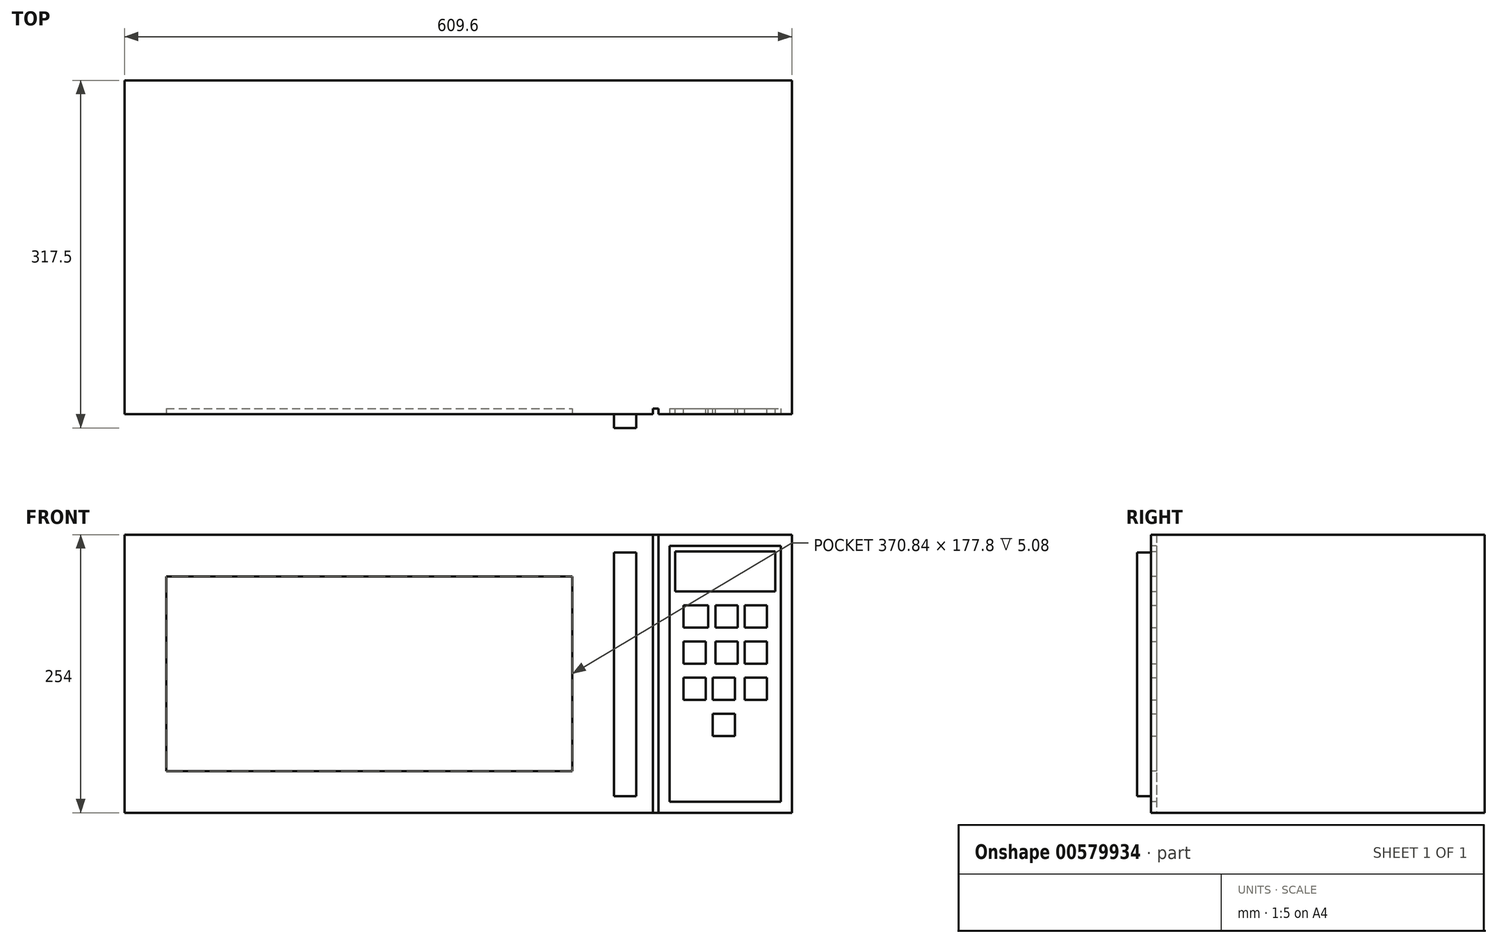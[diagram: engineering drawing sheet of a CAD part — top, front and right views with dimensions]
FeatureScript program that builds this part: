
annotation { "Feature Type Name" : "Feature", "Feature Type Description" : "" }
export const myFeature = defineFeature(function(context is Context, id is Id, definition is map)
    precondition{}
    {
        {
            var Q0;
            Q0=qCreatedBy(makeId("Front.planeOp"),FACE);
            var sketch = newSketch(context, id + "F0", { "sketchPlane" : qUnion([Q0])});
            skLineSegment(sketch, "E0.bottom", {"start": v(-322.23, 150.32) * mm, "end": v(287.37, 150.32) * mm});
            skLineSegment(sketch, "E0.top", {"start": v(-322.23, -103.68) * mm, "end": v(287.37, -103.68) * mm});
            skLineSegment(sketch, "E0.left", {"start": v(-322.23, 150.32) * mm, "end": v(-322.23, -103.68) * mm});
            skLineSegment(sketch, "E0.right", {"start": v(287.37, 150.32) * mm, "end": v(287.37, -103.68) * mm});
            skSolve(sketch);
        }
        {
            var Q0;
            Q0 = qSketchRegion(id + "F0", true);
            extrude(context, id + "F1", {"entities" : qUnion([Q0]), "depth" : 304.8 * mm, "offsetDistance" : 25.4 * mm});
        }
        {
            var Q0;
            Q0=makeQuery(id+"F1.opExtrude","CAP_FACE",FACE,{"disambiguationData":[OSD([sQuery(id+"F0.wireOp",EDGE,"E0.bottom"),sQuery(id+"F0.wireOp",EDGE,"E0.top"),sQuery(id+"F0.wireOp",EDGE,"E0.left"),sQuery(id+"F0.wireOp",EDGE,"E0.right")])],"isStart":false});
            var sketch = newSketch(context, id + "F2", { "sketchPlane" : qUnion([Q0])});
            skLineSegment(sketch, "E1.bottom", {"start": v(175.6, 140.16) * mm, "end": v(277.2, 140.16) * mm});
            skLineSegment(sketch, "E1.top", {"start": v(175.6, -93.52) * mm, "end": v(277.2, -93.52) * mm});
            skLineSegment(sketch, "E1.left", {"start": v(175.6, 140.16) * mm, "end": v(175.6, -93.52) * mm});
            skLineSegment(sketch, "E1.right", {"start": v(277.2, 140.16) * mm, "end": v(277.2, -93.52) * mm});
            skSolve(sketch);
        }
        {
            var Q0;
            Q0 = qSketchRegion(id + "F2", true);
            extrude(context, id + "F3", {"entities" : qUnion([Q0]), "operationType" : NewBodyOperationType.REMOVE, "oppositeDirection" : true, "depth" : 5.08 * mm, "offsetDistance" : 25.4 * mm});
        }
        {
            var Q0;
            Q0=makeQuery(id+"F1.opExtrude","CAP_FACE",FACE,{"disambiguationData":[OSD([sQuery(id+"F0.wireOp",EDGE,"E0.bottom"),sQuery(id+"F0.wireOp",EDGE,"E0.top"),sQuery(id+"F0.wireOp",EDGE,"E0.left"),sQuery(id+"F0.wireOp",EDGE,"E0.right")])],"isStart":false});
            var sketch = newSketch(context, id + "F4", { "sketchPlane" : qUnion([Q0])});
            skLineSegment(sketch, "E2.left", {"start": v(160.37, 150.32) * mm, "end": v(160.37, -103.68) * mm});
            skLineSegment(sketch, "E2.right", {"start": v(165.45, 150.32) * mm, "end": v(165.45, -103.68) * mm});
            skLineSegment(sketch, "E3", {"start": v(160.37, 150.32) * mm, "end": v(165.45, 150.32) * mm});
            skLineSegment(sketch, "E4", {"start": v(160.37, -103.68) * mm, "end": v(165.45, -103.68) * mm});
            skSolve(sketch);
        }
        {
            var Q0;
            Q0=makeQuery(id+"F4.imprint","IMPRINT",FACE,{"disambiguationData":[TD([[makeQuery(id+"F4.imprint","IMPRINT",EDGE,{"derivedFrom":sQuery(id+"F4.wireOp",EDGE,"E2.left")}),1.0]])]});
            extrude(context, id + "F5", {"entities" : qUnion([Q0]), "operationType" : NewBodyOperationType.REMOVE, "oppositeDirection" : true, "depth" : 5.08 * mm, "offsetDistance" : 25.4 * mm});
        }
        {
            var Q0;
            Q0=makeQuery(id+"F3.boolean.opBoolean","COPY",FACE,{"derivedFrom":makeQuery(id+"F3.opExtrude","CAP_FACE",FACE,{"disambiguationData":[OSD([sQuery(id+"F2.wireOp",EDGE,"E1.bottom"),sQuery(id+"F2.wireOp",EDGE,"E1.top"),sQuery(id+"F2.wireOp",EDGE,"E1.left"),sQuery(id+"F2.wireOp",EDGE,"E1.right")])],"isStart":false})});
            var sketch = newSketch(context, id + "F6", { "sketchPlane" : qUnion([Q0])});
            skLineSegment(sketch, "E5.bottom", {"start": v(180.69, 135.08) * mm, "end": v(272.13, 135.08) * mm});
            skLineSegment(sketch, "E5.top", {"start": v(180.69, 98.46) * mm, "end": v(272.13, 98.46) * mm});
            skLineSegment(sketch, "E5.left", {"start": v(180.69, 135.08) * mm, "end": v(180.69, 98.46) * mm});
            skLineSegment(sketch, "E5.right", {"start": v(272.13, 135.08) * mm, "end": v(272.13, 98.46) * mm});
            skLineSegment(sketch, "E6.bottom", {"start": v(188.3, 85.76) * mm, "end": v(210.92, 85.76) * mm});
            skLineSegment(sketch, "E6.top", {"start": v(188.3, 65.44) * mm, "end": v(210.92, 65.44) * mm});
            skLineSegment(sketch, "E6.left", {"start": v(188.3, 85.76) * mm, "end": v(188.3, 65.44) * mm});
            skLineSegment(sketch, "E6.right", {"start": v(210.92, 85.76) * mm, "end": v(210.92, 65.44) * mm});
            skLineSegment(sketch, "E7.bottom", {"start": v(217.52, 85.76) * mm, "end": v(237.84, 85.76) * mm});
            skLineSegment(sketch, "E7.top", {"start": v(217.52, 65.44) * mm, "end": v(237.84, 65.44) * mm});
            skLineSegment(sketch, "E7.left", {"start": v(217.52, 85.76) * mm, "end": v(217.52, 65.44) * mm});
            skLineSegment(sketch, "E7.right", {"start": v(237.84, 85.76) * mm, "end": v(237.84, 65.44) * mm});
            skLineSegment(sketch, "E8.bottom", {"start": v(244.19, 85.76) * mm, "end": v(264.5, 85.76) * mm});
            skLineSegment(sketch, "E8.top", {"start": v(244.19, 65.44) * mm, "end": v(264.5, 65.44) * mm});
            skLineSegment(sketch, "E8.left", {"start": v(244.19, 85.76) * mm, "end": v(244.19, 65.44) * mm});
            skLineSegment(sketch, "E8.right", {"start": v(264.5, 85.76) * mm, "end": v(264.5, 65.44) * mm});
            skLineSegment(sketch, "E9.bottom", {"start": v(188.3, 52.74) * mm, "end": v(208.63, 52.74) * mm});
            skLineSegment(sketch, "E9.top", {"start": v(188.3, 32.42) * mm, "end": v(208.63, 32.42) * mm});
            skLineSegment(sketch, "E9.left", {"start": v(188.3, 52.74) * mm, "end": v(188.3, 32.42) * mm});
            skLineSegment(sketch, "E9.right", {"start": v(208.63, 52.74) * mm, "end": v(208.63, 32.42) * mm});
            skLineSegment(sketch, "E10.bottom", {"start": v(217.52, 52.74) * mm, "end": v(237.84, 52.74) * mm});
            skLineSegment(sketch, "E10.top", {"start": v(217.52, 32.42) * mm, "end": v(237.84, 32.42) * mm});
            skLineSegment(sketch, "E10.left", {"start": v(217.52, 52.74) * mm, "end": v(217.52, 32.42) * mm});
            skLineSegment(sketch, "E10.right", {"start": v(237.84, 52.74) * mm, "end": v(237.84, 32.42) * mm});
            skLineSegment(sketch, "E11.bottom", {"start": v(244.19, 52.74) * mm, "end": v(264.5, 52.74) * mm});
            skLineSegment(sketch, "E11.top", {"start": v(244.19, 32.42) * mm, "end": v(264.5, 32.42) * mm});
            skLineSegment(sketch, "E11.left", {"start": v(244.19, 52.74) * mm, "end": v(244.19, 32.42) * mm});
            skLineSegment(sketch, "E11.right", {"start": v(264.5, 52.74) * mm, "end": v(264.5, 32.42) * mm});
            skLineSegment(sketch, "E12.bottom", {"start": v(188.3, 19.72) * mm, "end": v(208.63, 19.72) * mm});
            skLineSegment(sketch, "E12.top", {"start": v(188.3, -0.6) * mm, "end": v(208.63, -0.6) * mm});
            skLineSegment(sketch, "E12.left", {"start": v(188.3, 19.72) * mm, "end": v(188.3, -0.6) * mm});
            skLineSegment(sketch, "E12.right", {"start": v(208.63, 19.72) * mm, "end": v(208.63, -0.6) * mm});
            skLineSegment(sketch, "E13.bottom", {"start": v(215.23, 19.72) * mm, "end": v(235.55, 19.72) * mm});
            skLineSegment(sketch, "E13.top", {"start": v(215.23, -0.6) * mm, "end": v(235.55, -0.6) * mm});
            skLineSegment(sketch, "E13.left", {"start": v(215.23, 19.72) * mm, "end": v(215.23, -0.6) * mm});
            skLineSegment(sketch, "E13.right", {"start": v(235.55, 19.72) * mm, "end": v(235.55, -0.6) * mm});
            skLineSegment(sketch, "E14.bottom", {"start": v(244.19, 19.72) * mm, "end": v(264.5, 19.72) * mm});
            skLineSegment(sketch, "E14.top", {"start": v(244.19, -0.6) * mm, "end": v(264.5, -0.6) * mm});
            skLineSegment(sketch, "E14.left", {"start": v(244.19, 19.72) * mm, "end": v(244.19, -0.6) * mm});
            skLineSegment(sketch, "E14.right", {"start": v(264.5, 19.72) * mm, "end": v(264.5, -0.6) * mm});
            skLineSegment(sketch, "E15.bottom", {"start": v(214.98, -13.3) * mm, "end": v(235.3, -13.3) * mm});
            skLineSegment(sketch, "E15.top", {"start": v(214.98, -33.62) * mm, "end": v(235.3, -33.62) * mm});
            skLineSegment(sketch, "E15.left", {"start": v(214.98, -13.3) * mm, "end": v(214.98, -33.62) * mm});
            skLineSegment(sketch, "E15.right", {"start": v(235.3, -13.3) * mm, "end": v(235.3, -33.62) * mm});
            skSolve(sketch);
        }
        {
            var Q0;
            Q0 = qSketchRegion(id + "F6", true);
            extrude(context, id + "F7", {"entities" : qUnion([Q0]), "operationType" : NewBodyOperationType.ADD, "depth" : 5.08 * mm, "offsetDistance" : 25.4 * mm});
        }
        {
            var Q0;
            {var subQ0=sQuery(id+"F0.wireOp",EDGE,"E0.bottom");var subQ1=sQuery(id+"F0.wireOp",EDGE,"E0.top");var subQ2=sQuery(id+"F0.wireOp",EDGE,"E0.left");Q0=makeQuery(id+"F5.boolean.opBoolean","SPLIT",FACE,{"disambiguationData":[TD([makeQuery(id+"F1.opExtrude","SWEPT_FACE",FACE,{"disambiguationData":[OSD([subQ2])]})])],"derivedFrom":makeQuery(id+"F1.opExtrude","CAP_FACE",FACE,{"disambiguationData":[OSD([subQ0,subQ1,subQ2,sQuery(id+"F0.wireOp",EDGE,"E0.right")])],"isStart":false})});}
            var sketch = newSketch(context, id + "F8", { "sketchPlane" : qUnion([Q0])});
            skLineSegment(sketch, "E16.bottom", {"start": v(124.8, 134.1) * mm, "end": v(145.13, 134.1) * mm});
            skLineSegment(sketch, "E16.top", {"start": v(124.8, -88.44) * mm, "end": v(145.13, -88.44) * mm});
            skLineSegment(sketch, "E16.left", {"start": v(124.8, 134.1) * mm, "end": v(124.8, -88.44) * mm});
            skLineSegment(sketch, "E16.right", {"start": v(145.13, 134.1) * mm, "end": v(145.13, -88.44) * mm});
            skSolve(sketch);
        }
        {
            var Q0;
            Q0 = qSketchRegion(id + "F8", true);
            extrude(context, id + "F9", {"entities" : qUnion([Q0]), "operationType" : NewBodyOperationType.ADD, "depth" : 12.7 * mm, "offsetDistance" : 25.4 * mm});
        }
        {
            var Q0;
            {var subQ0=sQuery(id+"F0.wireOp",EDGE,"E0.bottom");var subQ1=sQuery(id+"F0.wireOp",EDGE,"E0.top");var subQ2=sQuery(id+"F0.wireOp",EDGE,"E0.left");Q0=makeQuery(id+"F5.boolean.opBoolean","SPLIT",FACE,{"disambiguationData":[TD([makeQuery(id+"F1.opExtrude","SWEPT_FACE",FACE,{"disambiguationData":[OSD([subQ2])]})])],"derivedFrom":makeQuery(id+"F1.opExtrude","CAP_FACE",FACE,{"disambiguationData":[OSD([subQ0,subQ1,subQ2,sQuery(id+"F0.wireOp",EDGE,"E0.right")])],"isStart":false})});}
            var sketch = newSketch(context, id + "F10", { "sketchPlane" : qUnion([Q0])});
            skLineSegment(sketch, "E17.bottom", {"start": v(-284.13, 112.22) * mm, "end": v(86.7, 112.22) * mm});
            skLineSegment(sketch, "E17.top", {"start": v(-284.13, -65.58) * mm, "end": v(86.7, -65.58) * mm});
            skLineSegment(sketch, "E17.left", {"start": v(-284.13, 112.22) * mm, "end": v(-284.13, -65.58) * mm});
            skLineSegment(sketch, "E17.right", {"start": v(86.7, 112.22) * mm, "end": v(86.7, -65.58) * mm});
            skSolve(sketch);
        }
        {
            var Q0;
            Q0 = qSketchRegion(id + "F10", true);
            extrude(context, id + "F11", {"entities" : qUnion([Q0]), "operationType" : NewBodyOperationType.REMOVE, "oppositeDirection" : true, "depth" : 5.08 * mm, "offsetDistance" : 25.4 * mm});
        }
    });
